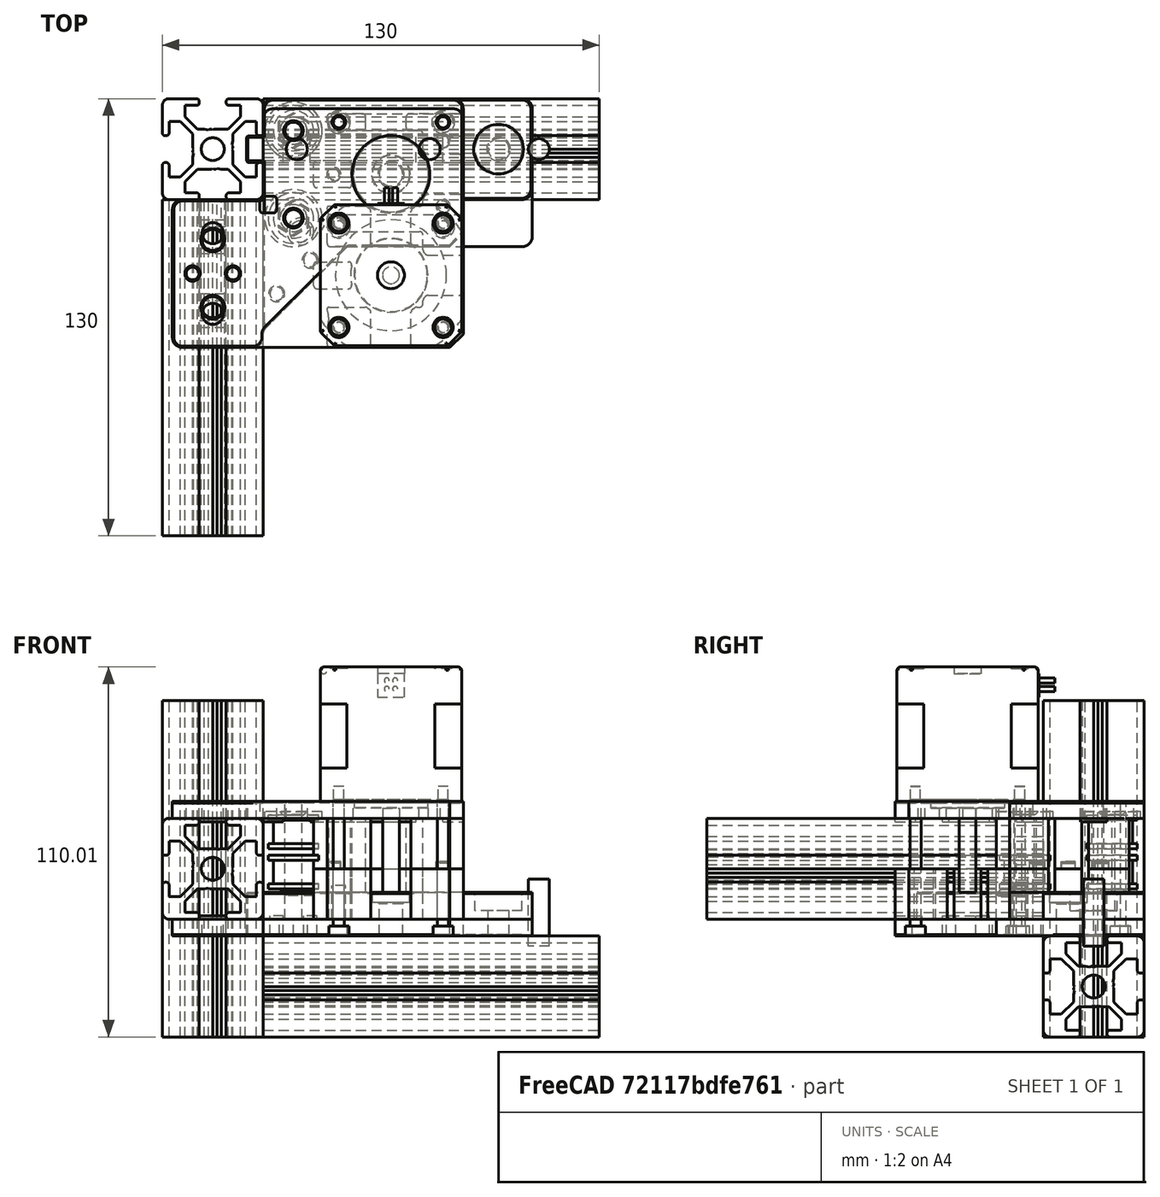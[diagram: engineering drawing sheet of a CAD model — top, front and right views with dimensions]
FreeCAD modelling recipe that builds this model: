
FCSTD DOCUMENT  (FreeCAD 0.19R24366 (Git))
Label: motor-mount-common
License: Other
LicenseURL: GPL3
objects: Part::Cylinder×38, Part::MultiFuse×31, Part::Box×30, Part::Feature×26, Part::Cut×24, Part::Chamfer×18, Part::Fillet×15, App::Part×2, Part::Refine×2, App::DocumentObjectGroup×1
note: 184 computed .brp shape members not serialized (recipe doc carries the construction recipe); baked Part::Feature solids carry a one-line shape summary decoded from their .brp

FEATURE [Part::Feature] Extrude001003002002002002  label="Extrude001003002002004"
  Placement = pos=(-15,-100,15) rot=(-1,0,0;1.5708rad)
  shape: bbox 30 x 100 x 30 mm, 95 faces (baked)
FEATURE [Part::Feature] Extrude001003002002002003  label="Extrude001003002002005"
  Placement = pos=(-2.5e-14,15,-20) rot=(0.57735,-0.57735,0.57735;4.18879rad)
  shape: bbox 100 x 30 x 30 mm, 95 faces (baked)
FEATURE [Part::Feature] Chamfer004  label="btm-support"
  Placement = pos=(11,-9.5,7) rot=(0,0,1;0rad)
  shape: bbox 8 x 8 x 1.85 mm, 4 faces (baked)
FEATURE [Part::Feature] Fusion006002011004053036004001001  label="motor-40mm"
  Placement = pos=(38,-22.5,75) rot=(1,0,0;3.14159rad)
  shape: bbox 42 x 47 x 67 mm, 100 faces (baked)
FEATURE [Part::Cylinder] Cylinder054
  Angle = 360
  AttacherType = Attacher::AttachEngine3D
  Height = 10
  Placement = pos=(22.5,-7,0) rot=(0,0,1;0rad)
  Radius = 2
FEATURE [Part::Box] Box  label="Cube"
  AttacherType = Attacher::AttachEngine3D
  Height = 5
  Length = 86.5
  Placement = pos=(-27,-44,30) rot=(0,0,1;0rad)
  Width = 44
FEATURE [Part::Feature] Cut001  label="smooth-idler-6mm"
  Placement = pos=(9,20.5,21) rot=(0,0,-1;1.5708rad)
  shape: bbox 15 x 15 x 10 mm, 8 faces (baked)
FEATURE [Part::Feature] Cut002005  label="smooth-idler-6mm004"
  Placement = pos=(9,20.5,9) rot=(0,0,-1;1.5708rad)
  shape: bbox 15 x 15 x 10 mm, 8 faces (baked)
FEATURE [Part::Feature] Cut002007  label="smooth-idler-6mm006"
  Placement = pos=(9,-5.5,9) rot=(0,0,-1;1.5708rad)
  shape: bbox 15 x 15 x 10 mm, 8 faces (baked)
FEATURE [App::Part] Part001  label="pref"
  Group = -> [Fusion006002011004053036004001001,Cut001,Cut002005,Cut002007]
  Origin = -> Origin001
FEATURE [Part::Box] Box001  label="Cube001"
  AttacherType = Attacher::AttachEngine3D
  Height = 5
  Length = 59.5
  Placement = pos=(0,0,30) rot=(0,0,1;0rad)
  Width = 27
FEATURE [Part::Box] Box002  label="Cube002"
  AttacherType = Attacher::AttachEngine3D
  Height = 5
  Length = 5
  Placement = pos=(-1,-4,30) rot=(0,0,1;0rad)
  Width = 5
FEATURE [Part::MultiFuse] Fusion
  Shapes = -> [Box,Box001]
FEATURE [Part::Cut] Cut
  Base = -> Fusion
  Tool = -> Box002
FEATURE [Part::Chamfer] Chamfer
  Base = -> Cut
  Edges = 1 edges r=4: [Edge6]
FEATURE [Part::Fillet] Fillet
  Base = -> Chamfer
  Edges = 4 edges r=3: [Edge3,Edge16,Edge38,Edge39]
FEATURE [Part::Fillet] Fillet001  label="base-plate-nh"
  Base = -> Fillet
  Edges = 5 edges r=1: [Edge37,Edge38,Edge40,Edge41,Edge50]
FEATURE [Part::Cylinder] Cylinder
  Angle = 360
  AttacherType = Attacher::AttachEngine3D
  Height = 10
  Placement = pos=(-15,-10,26.5) rot=(0,0,1;0rad)
  Radius = 3.15
FEATURE [Part::Cylinder] Cylinder055
  Angle = 360
  AttacherType = Attacher::AttachEngine3D
  Height = 10
  Placement = pos=(10,15,26.5) rot=(0,0,1;0rad)
  Radius = 3.15
FEATURE [Part::Cylinder] Cylinder056
  Angle = 360
  AttacherType = Attacher::AttachEngine3D
  Height = 10
  Placement = pos=(-15,-34,26.5) rot=(0,0,1;0rad)
  Radius = 3.15
FEATURE [Part::Cylinder] Cylinder057
  Angle = 360
  AttacherType = Attacher::AttachEngine3D
  Height = 10
  Placement = pos=(49.5,15,26.5) rot=(0,0,1;0rad)
  Radius = 3.15
FEATURE [Part::MultiFuse] Fusion006002011004053036004001002
  Shapes = -> [Cylinder057,Cylinder056,Cylinder055,Cylinder]
FEATURE [Part::Box] Box003  label="Cube003"
  AttacherType = Attacher::AttachEngine3D
  Height = 1
  Length = 6
  Placement = pos=(0,11.1,29) rot=(0,0,1;0rad)
  Width = 7.8
FEATURE [Part::Box] Box004  label="Cube004"
  AttacherType = Attacher::AttachEngine3D
  Height = 1
  Length = 6
  Placement = pos=(53.5,11.1,29) rot=(0,0,1;0rad)
  Width = 7.8
FEATURE [Part::Box] Box005  label="Cube005"
  AttacherType = Attacher::AttachEngine3D
  Height = 1
  Length = 31.5
  Placement = pos=(14,11.1,29) rot=(0,0,1;0rad)
  Width = 7.8
FEATURE [Part::Box] Box006  label="Cube006"
  AttacherType = Attacher::AttachEngine3D
  Height = 1
  Length = 7.8
  Placement = pos=(-18.9,-6,29) rot=(0,0,1;0rad)
  Width = 6
FEATURE [Part::Box] Box007  label="Cube007"
  AttacherType = Attacher::AttachEngine3D
  Height = 1
  Length = 7.8
  Placement = pos=(-18.9,-44,29) rot=(0,0,1;0rad)
  Width = 6
FEATURE [Part::Box] Box008  label="Cube008"
  AttacherType = Attacher::AttachEngine3D
  Height = 1
  Length = 7.8
  Placement = pos=(-18.9,-30,29) rot=(0,0,1;0rad)
  Width = 15.5
FEATURE [Part::MultiFuse] Fusion006002011004053036004001003  label="mounting-tab"
  Shapes = -> [Box008,Box007,Box006,Box005,Box004,Box003]
FEATURE [Part::Cut] Cut002008  label="base-plate"
  Base = -> Fillet001
  Tool = -> Fusion006002011004053036004001002
FEATURE [Part::Box] Box009  label="Cube009"
  AttacherType = Attacher::AttachEngine3D
  Height = 8
  Length = 80
  Placement = pos=(0,-14,0) rot=(0,0,1;0rad)
  Width = 44
FEATURE [Part::Feature] Chamfer009  label="btm-support001"
  Placement = pos=(9,20.5,7) rot=(0,0,1;0rad)
  shape: bbox 8 x 8 x 1.85 mm, 4 faces (baked)
FEATURE [Part::Feature] Chamfer010  label="top-support001"
  Placement = pos=(9,20.5,33) rot=(0,0,1;0rad)
  shape: bbox 8 x 8 x 1.85 mm, 4 faces (baked)
FEATURE [Part::Cylinder] Cylinder058
  Angle = 360
  AttacherType = Attacher::AttachEngine3D
  Height = 3
  Placement = pos=(9,20.5,29) rot=(0,0,1;0rad)
  Radius = 8.5
FEATURE [Part::Cylinder] Cylinder059
  Angle = 360
  AttacherType = Attacher::AttachEngine3D
  Height = 4
  Placement = pos=(38,7.5,5) rot=(0,0,1;0rad)
  Radius = 5.55
FEATURE [Part::Cylinder] Cylinder060
  Angle = 360
  AttacherType = Attacher::AttachEngine3D
  Height = 9
  Placement = pos=(38,7.5,28.5) rot=(0,0,1;0rad)
  Radius = 11.15
FEATURE [Part::Cylinder] Cylinder061
  Angle = 360
  AttacherType = Attacher::AttachEngine3D
  Height = 40
  Placement = pos=(22.5,-7,-5) rot=(0,0,1;0rad)
  Radius = 1.65
FEATURE [Part::Cylinder] Cylinder062
  Angle = 360
  AttacherType = Attacher::AttachEngine3D
  Height = 40
  Placement = pos=(53.5,-7,-5) rot=(0,0,1;0rad)
  Radius = 1.65
FEATURE [Part::Cylinder] Cylinder063
  Angle = 360
  AttacherType = Attacher::AttachEngine3D
  Height = 40
  Placement = pos=(22.5,-38,-5) rot=(0,0,1;0rad)
  Radius = 1.65
FEATURE [Part::Cylinder] Cylinder064
  Angle = 360
  AttacherType = Attacher::AttachEngine3D
  Height = 40
  Placement = pos=(53.5,-38,-5) rot=(0,0,1;0rad)
  Radius = 1.65
FEATURE [Part::Cylinder] Cylinder065
  Angle = 360
  AttacherType = Attacher::AttachEngine3D
  Height = 3
  Placement = pos=(22.5,-7,-5) rot=(0,0,1;0rad)
  Radius = 3
FEATURE [Part::Cylinder] Cylinder066
  Angle = 360
  AttacherType = Attacher::AttachEngine3D
  Height = 3
  Placement = pos=(53.5,-7,-5) rot=(0,0,1;0rad)
  Radius = 3
FEATURE [Part::Cylinder] Cylinder067
  Angle = 360
  AttacherType = Attacher::AttachEngine3D
  Height = 3
  Placement = pos=(22.5,-38,-5) rot=(0,0,1;0rad)
  Radius = 3
FEATURE [Part::Cylinder] Cylinder068
  Angle = 360
  AttacherType = Attacher::AttachEngine3D
  Height = 3
  Placement = pos=(53.5,-38,-5) rot=(0,0,1;0rad)
  Radius = 3
FEATURE [Part::MultiFuse] Fusion006002011004053036004001003009  label="motor-bolt"
  Shapes = -> [Cylinder068,Cylinder067,Cylinder066,Cylinder065,Cylinder061,Cylinder062,Cylinder063,Cylinder064]
FEATURE [Part::Box] Box011  label="Cube011"
  AttacherType = Attacher::AttachEngine3D
  Height = 15
  Length = 13
  Placement = pos=(19,-44,0) rot=(0,0,1;0rad)
  Width = 12
FEATURE [Part::Box] Box012  label="Cube012"
  AttacherType = Attacher::AttachEngine3D
  Height = 15
  Length = 15.5
  Placement = pos=(44,-44,0) rot=(0,0,1;0rad)
  Width = 12
FEATURE [Part::Box] Box013  label="Cube013"
  AttacherType = Attacher::AttachEngine3D
  Height = 15
  Length = 40.5
  Placement = pos=(19,-9.5,0) rot=(0,0,1;0rad)
  Width = 5
FEATURE [Part::Box] Box014  label="Cube014"
  AttacherType = Attacher::AttachEngine3D
  Height = 15
  Length = 12
  Placement = pos=(47.5,-32,0) rot=(0,0,1;0rad)
  Width = 3.5
FEATURE [Part::Chamfer] Chamfer012
  Base = -> Box012
  Edges = 1 edges r=4: [Edge5]
FEATURE [Part::Box] Box015  label="Cube015"
  AttacherType = Attacher::AttachEngine3D
  Height = 15
  Length = 12
  Placement = pos=(47.5,-16.5,0) rot=(0,0,1;0rad)
  Width = 7
FEATURE [Part::Cylinder] Cylinder069
  Angle = 360
  AttacherType = Attacher::AttachEngine3D
  Height = 15
  Placement = pos=(11,-35.5,0) rot=(0,0,1;0rad)
  Radius = 8.5
FEATURE [Part::Cylinder] Cylinder070
  Angle = 360
  AttacherType = Attacher::AttachEngine3D
  Height = 15
  Placement = pos=(38,-22.5,0) rot=(0,0,1;0rad)
  Radius = 12
FEATURE [Part::Cylinder] Cylinder071
  Angle = 360
  AttacherType = Attacher::AttachEngine3D
  Height = 15
  Placement = pos=(11,-9.5,0) rot=(0,0,1;0rad)
  Radius = 8.5
FEATURE [Part::MultiFuse] Fusion006002011004053036004001003011
  Shapes = -> [Cylinder070,Cylinder069,Cylinder071]
FEATURE [Part::Box] Box016  label="Cube016"
  AttacherType = Attacher::AttachEngine3D
  Height = 15
  Length = 14.5
  Placement = pos=(15,-26.5,0) rot=(0,0,1;0rad)
  Width = 8
FEATURE [Part::MultiFuse] Fusion006002011004053036004001003012
  Shapes = -> [Box013,Box015,Box014,Chamfer012,Box011,Box016]
FEATURE [Part::Cut] Cut002008008
  Base = -> Fusion006002011004053036004001003012
  Tool = -> Fusion006002011004053036004001003011
FEATURE [Part::Fillet] Fillet003
  Base = -> Cut002008008
  Edges = 1 edges r=0.5: [Edge83]
FEATURE [Part::Fillet] Fillet004  label="wall"
  Base = -> Fillet003
  Edges = 23 edges r=1: [Edge18,Edge21,Edge24,Edge26,Edge29,Edge31,Edge38,Edge43,Edge49,Edge54,Edge55,Edge56,Edge58,Edge60,Edge65,Edge72,Edge73,Edge85,Edge88,Edge89,Edge91,Edge94,Edge99]
FEATURE [App::DocumentObjectGroup] Group  label="Base"
  Group = -> [Cut002008,Fusion006002011004053036004001003,Fillet004,Fusion006002011004053036004001003009]
FEATURE [Part::Cylinder] Cylinder072
  Angle = 360
  AttacherType = Attacher::AttachEngine3D
  Height = 2.2
  Placement = pos=(21,-22.5,15) rot=(0,0,1;0rad)
  Radius = 2.1
FEATURE [Part::Cylinder] Cylinder073
  Angle = 360
  AttacherType = Attacher::AttachEngine3D
  Height = 2.2
  Placement = pos=(53.5,-32,15) rot=(0,0,1;0rad)
  Radius = 2.1
FEATURE [Part::Cylinder] Cylinder074
  Angle = 360
  AttacherType = Attacher::AttachEngine3D
  Height = 2.2
  Placement = pos=(53.5,-12.5,15) rot=(0,0,1;0rad)
  Radius = 2.1
FEATURE [Part::Cylinder] Cylinder075
  Angle = 360
  AttacherType = Attacher::AttachEngine3D
  Height = 2
  Placement = pos=(53.5,-12.5,15) rot=(0,0,1;0rad)
  Radius = 2
FEATURE [Part::Cylinder] Cylinder076
  Angle = 360
  AttacherType = Attacher::AttachEngine3D
  Height = 2
  Placement = pos=(53.5,-32,15) rot=(0,0,1;0rad)
  Radius = 2
FEATURE [Part::Cylinder] Cylinder077
  Angle = 360
  AttacherType = Attacher::AttachEngine3D
  Height = 2
  Placement = pos=(21,-22.5,15) rot=(0,0,1;0rad)
  Radius = 2
FEATURE [Part::MultiFuse] Fusion006002011004053036004001003013
  Shapes = -> [Cylinder077,Cylinder076,Cylinder075]
FEATURE [Part::Chamfer] Chamfer013
  Base = -> Fusion006002011004053036004001003013
  Edges = 3 edges r=0.4: [Edge1,Edge4,Edge7]
FEATURE [Part::MultiFuse] Fusion006002011004053036004001003014
  Shapes = -> [Cylinder074,Cylinder072,Cylinder073]
FEATURE [Part::Feature] Fillet004001  label="wall001"
  shape: bbox 44.5 x 39.5 x 15 mm, 60 faces, 4 solids (baked)
FEATURE [Part::Feature] Fillet004002  label="wall002"
  Placement = pos=(0,0,15) rot=(0,0,1;0rad)
  shape: bbox 44.5 x 39.5 x 15 mm, 60 faces, 4 solids (baked)
FEATURE [Part::Cut] Cut002008009  label="upper-wall"
  Base = -> Fillet004002
  Placement = pos=(0,30,0) rot=(0,0,1;0rad)
  Tool = -> Fusion006002011004053036004001003014
FEATURE [Part::Feature] Fusion006002011004053036004001003009001  label="motor-bolt001"
  Placement = pos=(0,30,0) rot=(0,0,1;0rad)
  shape: bbox 37 x 37 x 40 mm, 20 faces, 4 solids (baked)
FEATURE [Part::Feature] Fusion006002011004053036004001003009002  label="motor-bolt002"
  Placement = pos=(0,30,0) rot=(0,0,1;0rad)
  shape: bbox 37 x 37 x 40 mm, 20 faces, 4 solids (baked)
FEATURE [Part::Feature] Chamfer015  label="btm-support002"
  Placement = pos=(9,-5.5,7) rot=(0,0,1;0rad)
  shape: bbox 8 x 8 x 1.85 mm, 4 faces (baked)
FEATURE [Part::Cylinder] Cylinder078
  Angle = 360
  AttacherType = Attacher::AttachEngine3D
  Height = 10
  Placement = pos=(9,-5.5,22) rot=(0,0,1;0rad)
  Radius = 8.5
FEATURE [Part::Feature] Chamfer014  label="top-support002"
  Placement = pos=(9,-5.5,33) rot=(0,0,1;0rad)
  shape: bbox 8 x 8 x 1.85 mm, 4 faces (baked)
FEATURE [Part::Cylinder] Cylinder079
  Angle = 360
  AttacherType = Attacher::AttachEngine3D
  Height = 44
  Placement = pos=(9,20.5,-10) rot=(0,0,1;0rad)
  Radius = 2.525
FEATURE [Part::Cylinder] Cylinder080
  Angle = 360
  AttacherType = Attacher::AttachEngine3D
  Height = 44
  Placement = pos=(9,-5.5,-10) rot=(0,0,1;0rad)
  Radius = 2.525
FEATURE [Part::Feature] Fusion006002011004053036004001003009006001  label="Fusion006002011004053036004001003009007"
  Placement = pos=(-2,30,-7) rot=(0,0,1;0rad)
  shape: bbox 5.05 x 31.05 x 44 mm, 6 faces, 2 solids (baked)
FEATURE [Part::Feature] Body001  label="m5-nut-slot"
  Placement = pos=(9,20.5,-5) rot=(0,0,1;0rad)
  shape: bbox 8.4 x 9.7 x 4 mm, 8 faces (baked)
FEATURE [Part::Feature] Body002  label="m5-nut-slot001"
  Placement = pos=(9,-5.5,-5) rot=(0,0,1;0rad)
  shape: bbox 8.4 x 9.7 x 4 mm, 8 faces (baked)
FEATURE [Part::Feature] Extrude001003002002002001  label="Extrude001003002002003"
  Placement = pos=(-15,15,-35) rot=(0,0,1;0rad)
  shape: bbox 30 x 30 x 100 mm, 95 faces (baked)
FEATURE [App::Part] Part  label="extrusion"
  Group = -> [Extrude001003002002002001,Extrude001003002002002002,Extrude001003002002002003]
  Origin = -> Origin
FEATURE [Part::Box] Box018  label="Cube018"
  AttacherType = Attacher::AttachEngine3D
  Height = 5
  Length = 27
  Placement = pos=(-27,-44,-5) rot=(0,0,1;0rad)
  Width = 44
FEATURE [Part::Box] Box019  label="Cube019"
  AttacherType = Attacher::AttachEngine3D
  Height = 5
  Length = 80
  Placement = pos=(0,-14,-5) rot=(0,0,1;0rad)
  Width = 44
FEATURE [Part::MultiFuse] Fusion006002011004053036004001003009006003
  Shapes = -> [Box019,Box018]
FEATURE [Part::Chamfer] Chamfer016
  Base = -> Fusion006002011004053036004001003009006003
  Edges = 1 edges r=25: [Edge21]
FEATURE [Part::Fillet] Fillet004003
  Base = -> Chamfer016
  Edges = 6 edges r=3: [Edge10,Edge13,Edge20,Edge25,Edge28,Edge29]
FEATURE [Part::Box] Box020  label="Cube020"
  AttacherType = Attacher::AttachEngine3D
  Height = 8
  Length = 26
  Placement = pos=(-1,-39,0) rot=(0,0,1;0rad)
  Width = 26
FEATURE [Part::Box] Box021  label="Cube021"
  AttacherType = Attacher::AttachEngine3D
  Height = 8
  Length = 26
  Placement = pos=(-26,-39,0) rot=(0,0,1;0rad)
  Width = 26
FEATURE [Part::Chamfer] Chamfer017
  Base = -> Box020
  Edges = 1 edges r=25: [Edge5]
FEATURE [Part::Cut] Cut002008010
  Base = -> Chamfer017
  Tool = -> Box021
FEATURE [Part::Fillet] Fillet004003004
  Base = -> Cut002008010
  Edges = 1 edges r=1: [Edge9]
FEATURE [Part::MultiFuse] Fusion006002011004053036004001003009006004
  Shapes = -> [Fillet004003004,Box009]
FEATURE [Part::Fillet] Fillet004003005
  Base = -> Fusion006002011004053036004001003009006004
  Edges = 1 edges r=1.99: [Edge20]
FEATURE [Part::Box] Box022  label="Cube022"
  AttacherType = Attacher::AttachEngine3D
  Height = 5
  Length = 6
  Placement = pos=(-5,11.1,-5) rot=(0,0,1;0rad)
  Width = 7.8
FEATURE [Part::Box] Box023  label="Cube023"
  AttacherType = Attacher::AttachEngine3D
  Height = 8
  Length = 6
  Placement = pos=(-5,11.1,0) rot=(0,0,1;0rad)
  Width = 7.8
FEATURE [Part::Chamfer] Chamfer018
  Base = -> Box023
  Edges = 2 edges r=0.4: [Edge1,Edge3]
FEATURE [Part::Chamfer] Chamfer019
  Base = -> Box022
  Edges = 2 edges r=0.4: [Edge1,Edge3]
FEATURE [Part::Feature] Fusion006002011004053036004001003009006006001  label="base-plate002"
  Placement = pos=(0,0,35) rot=(0,0,1;0rad)
  shape: bbox 107 x 74 x 5 mm, 30 faces (baked)
FEATURE [Part::Box] Box024  label="Cube024"
  AttacherType = Attacher::AttachEngine3D
  Height = 10
  Length = 27
  Placement = pos=(59.5,-15,26) rot=(0,0,1;0rad)
  Width = 46
FEATURE [Part::Cut] Cut002008011
  Base = -> Fusion006002011004053036004001003009006006001
  Tool = -> Box024
FEATURE [Part::Chamfer] Chamfer021
  Base = -> Cut002008011
  Edges = 1 edges r=4: [Edge44]
FEATURE [Part::Fillet] Fillet004003007
  Base = -> Chamfer021
  Edges = 1 edges r=3: [Edge29]
FEATURE [Part::Box] Box025  label="Cube025"
  AttacherType = Attacher::AttachEngine3D
  Height = 1
  Length = 7.8
  Placement = pos=(-18.9,-44,0) rot=(0,0,1;0rad)
  Width = 8
FEATURE [Part::Cylinder] Cylinder081
  Angle = 360
  AttacherType = Attacher::AttachEngine3D
  Height = 47
  Placement = pos=(-15,-12,0) rot=(0,0,1;0rad)
  Radius = 3.15
FEATURE [Part::Cylinder] Cylinder082
  Angle = 360
  AttacherType = Attacher::AttachEngine3D
  Height = 47
  Placement = pos=(-15,-32,0) rot=(0,0,1;0rad)
  Radius = 3.15
FEATURE [Part::Box] Box026  label="Cube026"
  AttacherType = Attacher::AttachEngine3D
  Height = 1
  Length = 7.8
  Placement = pos=(-18.9,-28,0) rot=(0,0,1;0rad)
  Width = 12
FEATURE [Part::Box] Box027  label="Cube027"
  AttacherType = Attacher::AttachEngine3D
  Height = 1
  Length = 7.8
  Placement = pos=(-18.9,-8,0) rot=(0,0,1;0rad)
  Width = 8
FEATURE [Part::MultiFuse] Fusion006002011004053036004001003009006006002  label="mounting-tab001"
  Shapes = -> [Box027,Box026,Box025]
FEATURE [Part::MultiFuse] Fusion006002011004053036004001003009006006003
  Placement = pos=(0,0,-15) rot=(0,0,1;0rad)
  Shapes = -> [Cylinder081,Cylinder082]
FEATURE [Part::Feature] Fusion006002011004053036004001003009006006003001  label="Fusion006002011004053036004001003009006006004"
  shape: bbox 6.3 x 26.3 x 47 mm, 6 faces, 2 solids (baked)
FEATURE [Part::Feature] Fusion006002011004053036004001003009006006002001  label="mounting-tab002"
  Placement = pos=(0,0,29) rot=(0,0,1;0rad)
  shape: bbox 7.8 x 44 x 1 mm, 18 faces, 3 solids (baked)
FEATURE [Part::MultiFuse] Fusion006002011004053036004001003009006006003003
  Shapes = -> [Fusion006002011004053036004001003009006006002001,Fillet004003007]
FEATURE [Part::Cut] Cut002008013
  Base = -> Fusion006002011004053036004001003009006006003003
  Tool = -> Fusion006002011004053036004001003009006006003001
FEATURE [Part::Cylinder] Cylinder083
  Angle = 360
  AttacherType = Attacher::AttachEngine3D
  Height = 19
  Placement = pos=(70,15,-8.5) rot=(0,0,1;0rad)
  Radius = 3.1
FEATURE [Part::Box] Box028  label="Cube028"
  AttacherType = Attacher::AttachEngine3D
  Height = 22
  Length = 27
  Placement = pos=(59.5,-14,-7.5) rot=(0,0,1;0rad)
  Width = 14
FEATURE [Part::Box] Box029  label="Cube029"
  AttacherType = Attacher::AttachEngine3D
  Height = 22
  Length = 27
  Placement = pos=(59.5,-14,-7.5) rot=(0,0,1;0rad)
  Width = 14
FEATURE [Part::Cylinder] Cylinder084
  Angle = 360
  AttacherType = Attacher::AttachEngine3D
  Height = 20
  Placement = pos=(82,15,-8) rot=(0,0,1;0rad)
  Radius = 3.1
FEATURE [Part::MultiFuse] Fusion006002011004053036004001003015  label="lower-wall"
  Placement = pos=(0,30,0) rot=(0,0,1;0rad)
  Shapes = -> [Fillet004001,Chamfer013]
FEATURE [Part::Feature] Fillet004003001  label="Fillet004004"
  shape: bbox 107 x 74 x 5 mm, 17 faces (baked)
FEATURE [Part::Fillet] Fillet004003002
  Base = -> Fillet004003001
  Edges = 2 edges r=1.99: [Edge3,Edge9]
FEATURE [Part::Fillet] Fillet004003003
  Base = -> Fillet004003002
  Edges = 1 edges r=1: [Edge48]
FEATURE [Part::MultiFuse] Fusion006002011004053036004001003009006006  label="base-plate001"
  Shapes = -> [Fillet004003003,Chamfer019]
FEATURE [Part::MultiFuse] Fusion006002011004053036004001003009006006003002
  Shapes = -> [Fusion006002011004053036004001003009006006002,Fusion006002011004053036004001003009006006]
FEATURE [Part::Cut] Cut002008014
  Base = -> Fusion006002011004053036004001003009006006003002
  Tool = -> Fusion006002011004053036004001003009006006003
FEATURE [Part::Fillet] Fillet004003006
  Base = -> Fillet004003005
  Edges = 3 edges r=3: [Edge26,Edge27,Edge30]
FEATURE [Part::Cut] Cut002008023012003
  Base = -> Fillet004003006
  Tool = -> Box028
FEATURE [Part::Cut] Cut002008023012004
  Base = -> Cut002008014
  Tool = -> Box029
FEATURE [Part::Chamfer] Chamfer033
  Base = -> Cut002008023012003
  Edges = 1 edges r=4: [Edge34]
FEATURE [Part::Chamfer] Chamfer034
  Base = -> Cut002008023012004
  Edges = 1 edges r=4: [Edge53]
FEATURE [Part::Fillet] Fillet004003008
  Base = -> Chamfer033
  Edges = 1 edges r=3: [Edge20]
FEATURE [Part::Fillet] Fillet004003009
  Base = -> Chamfer034
  Edges = 1 edges r=3: [Edge38]
FEATURE [Part::Feature] Fillet004003008001  label="Fillet004003010"
  shape: bbox 80 x 67.59 x 8 mm, 15 faces (baked)
FEATURE [Part::Chamfer] Chamfer035
  Base = -> Fillet004003008001
  Edges = 13 edges r=0.4: [Edge4,Edge7,Edge8,Edge11,Edge16,Edge19,Edge22,Edge25,Edge28,Edge31,Edge34,Edge37,Edge38]
FEATURE [Part::Cylinder] Cylinder085
  Angle = 360
  AttacherType = Attacher::AttachEngine3D
  Height = 19
  Placement = pos=(70,15,2.5) rot=(0,0,1;0rad)
  Radius = 7
FEATURE [Part::MultiFuse] Fusion006002011004053036004001003009006006003012
  Shapes = -> [Cylinder085,Cylinder083]
FEATURE [Part::Chamfer] Chamfer038
  Base = -> Chamfer018
  Edges = 5 edges r=0.4: [Edge1,Edge5,Edge6,Edge7,Edge8]
FEATURE [Part::MultiFuse] Fusion006002011004053036004001003009006006003013
  Shapes = -> [Chamfer035,Chamfer038]
FEATURE [Part::MultiFuse] Fusion006002011004053036004001003009006006003014
  Shapes = -> [Fillet004003009,Fusion006002011004053036004001003009006006003013]
FEATURE [Part::MultiFuse] Fusion006002011004053036004001003009006006003015
  Shapes = -> [Fusion006002011004053036004001003009006006003014,Fusion006002011004053036004001003015]
FEATURE [Part::MultiFuse] Fusion006002011004053036004001003009006006003016
  Shapes = -> [Chamfer015,Chamfer009]
FEATURE [Part::MultiFuse] Fusion006002011004053036004001003009006006003017
  Shapes = -> [Fusion006002011004053036004001003009006006003015,Fusion006002011004053036004001003009006006003016]
FEATURE [Part::Cut] Cut002008023012005
  Base = -> Fusion006002011004053036004001003009006006003017
  Tool = -> Cylinder059
FEATURE [Part::MultiFuse] Fusion006002011004053036004001003009006006003018
  Shapes = -> [Body001,Body002]
FEATURE [Part::MultiFuse] Fusion006002011004053036004001003009006006003019
  Shapes = -> [Cylinder080,Cylinder079]
FEATURE [Part::Cut] Cut002008023012006
  Base = -> Cut002008023012005
  Tool = -> Fusion006002011004053036004001003009006006003019
FEATURE [Part::Cut] Cut002008023012007
  Base = -> Cut002008023012006
  Tool = -> Fusion006002011004053036004001003009001
FEATURE [Part::Cut] Cut002008023012008
  Base = -> Cut002008023012007
  Tool = -> Fusion006002011004053036004001003009006006003012
FEATURE [Part::Chamfer] Chamfer039
  Base = -> Cut002008023012008
  Edges = 1 edges r=0.2: [Edge280]
FEATURE [Part::Chamfer] Chamfer040
  Base = -> Chamfer039
  Edges = 1 edges r=0.4: [Edge67]
FEATURE [Part::MultiFuse] Fusion006002011004053036004001003009006006003020
  Shapes = -> [Cylinder078,Cylinder058]
FEATURE [Part::Cut] Cut002008023012009002
  Base = -> Cut002008013
  Tool = -> Fusion006002011004053036004001003009006006003020
FEATURE [Part::MultiFuse] Fusion006002011004053036004001003009006006003021
  Shapes = -> [Chamfer014,Chamfer010]
FEATURE [Part::MultiFuse] Fusion006002011004053036004001003009006006003022
  Shapes = -> [Cut002008023012009002,Fusion006002011004053036004001003009006006003021]
FEATURE [Part::Cut] Cut002008023012009003
  Base = -> Fusion006002011004053036004001003009006006003022
  Tool = -> Fusion006002011004053036004001003009006001
FEATURE [Part::Cut] Cut002008023012009005
  Base = -> Cut002008023012009003
  Tool = -> Cylinder060
FEATURE [Part::MultiFuse] Fusion006002011004053036004001003009006006003023
  Shapes = -> [Cut002008009,Cut002008023012009005]
FEATURE [Part::Cylinder] Cylinder086
  Angle = 360
  AttacherType = Attacher::AttachEngine3D
  Height = 6
  Placement = pos=(13,-19,-5) rot=(0,0,1;0rad)
  Radius = 2
FEATURE [Part::Cylinder] Cylinder087
  Angle = 360
  AttacherType = Attacher::AttachEngine3D
  Height = 6
  Placement = pos=(3,-29,-5) rot=(0,0,1;0rad)
  Radius = 2
FEATURE [Part::MultiFuse] Fusion006002011004053036004001003009006006003024
  Placement = pos=(1,1,0) rot=(0,0,1;0rad)
  Shapes = -> [Cylinder087,Cylinder086]
FEATURE [Part::Cylinder] Cylinder090
  Angle = 360
  AttacherType = Attacher::AttachEngine3D
  Height = 10
  Placement = pos=(-21,-22,35) rot=(0,0,1;0rad)
  Radius = 1.9
FEATURE [Part::Cylinder] Cylinder091
  Angle = 360
  AttacherType = Attacher::AttachEngine3D
  Height = 10
  Placement = pos=(-9,-22,35) rot=(0,0,1;0rad)
  Radius = 1.9
FEATURE [Part::MultiFuse] Fusion006002011004053036004001003009006006003025
  Placement = pos=(0,0,-5) rot=(0,0,1;0rad)
  Shapes = -> [Cylinder091,Cylinder090]
FEATURE [Part::Feature] Cut002008023012009006003002001  label="Cut002008023012009006003003"
  shape: bbox 86.5 x 74 x 20 mm, 140 faces (baked)
FEATURE [Part::Box] Box030  label="Cube030"
  AttacherType = Attacher::AttachEngine3D
  Height = 22
  Length = 12
  Placement = pos=(30.5,20.5,8) rot=(0,0,1;0rad)
  Width = 5
FEATURE [Part::Box] Box031  label="Cube031"
  AttacherType = Attacher::AttachEngine3D
  Height = 22
  Length = 12
  Placement = pos=(30.5,20.5,8) rot=(0,0,1;0rad)
  Width = 5
FEATURE [Part::Feature] Fusion006002011004053036004001003009006006003018001
  Placement = pos=(0,0,1) rot=(0,0,1;0rad)
  shape: bbox 8.4 x 35.7 x 4 mm, 16 faces, 2 solids (baked)
FEATURE [Part::MultiFuse] Fusion006002011004053036004001003009006006003018002
  Shapes = -> [Fusion006002011004053036004001003009006006003018001,Fusion006002011004053036004001003009006006003018]
FEATURE [Part::Cut] Cut002008023012009006003002003
  Base = -> Chamfer040
  Tool = -> Fusion006002011004053036004001003009006006003018002
FEATURE [Part::Cut] Cut002008023012009006003002004
  Base = -> Cut002008023012009006003002003
  Tool = -> Fusion006002011004053036004001003009006006003024
FEATURE [Part::Cut] Cut002008023012009006003002005
  Base = -> Cut002008023012009006003002004
  Tool = -> Box031
FEATURE [Part::Fillet] Fillet004003008003  label="btm-basic"
  Base = -> Cut002008023012009006003002005
  Edges = 4 edges r=1: [Edge191,Edge194,Edge198,Edge199]
FEATURE [Part::Cut] Cut002008023012009006003002006
  Base = -> Fusion006002011004053036004001003009006006003023
  Tool = -> Fusion006002011004053036004001003009002
FEATURE [Part::Cut] Cut002008023012009006003002007
  Base = -> Cut002008023012009006003002006
  Tool = -> Fusion006002011004053036004001003009006006003025
FEATURE [Part::Cut] Cut002008023012009006003002008
  Base = -> Cut002008023012009006003002007
  Tool = -> Box030
FEATURE [Part::Fillet] Fillet004003008004  label="top-basic"
  Base = -> Cut002008023012009006003002008
  Edges = 4 edges r=1: [Edge140,Edge145,Edge163,Edge166]
FEATURE [Part::Refine] Fillet004003008004001  label="top-basic001"
  Source = -> Fillet004003008004
FEATURE [Part::Refine] Fillet004003008003001  label="btm-basic001"
  Source = -> Fillet004003008003
FEATURE [Part::Chamfer] Chamfer041
  Base = -> Fillet004003008004001
  Edges = 25 edges r=0.4: [Edge202,Edge204,Edge206,Edge209,Edge210,Edge221,Edge223,Edge225,Edge235,Edge239,Edge241,Edge242,Edge244,Edge247,Edge248,Edge250,Edge252,Edge256,Edge257,Edge258,Edge334,Edge336,Edge337,Edge339,Edge340]
FEATURE [Part::Chamfer] Chamfer042
  Base = -> Fillet004003008003001
  Edges = 39 edges r=0.4: [Edge216,Edge220,Edge221,Edge230,Edge233,Edge235,Edge244,Edge381,Edge384,Edge386,Edge387,Edge389,Edge391,Edge393,Edge395,Edge398,Edge401,Edge404,Edge405,Edge407,Edge408,Edge409,Edge410,Edge411,Edge412,Edge413,Edge414,Edge415,Edge416,Edge417,Edge418,Edge419,Edge420,Edge421,Edge422,Edge423,Edge424,+2 more]
FEATURE [Part::Cylinder] Cylinder092
  Angle = 360
  AttacherType = Attacher::AttachEngine3D
  Height = 13
  Placement = pos=(38,7.5,-6.5) rot=(0,0,1;0rad)
  Radius = 3.5
FEATURE [Part::Cut] Cut002008023012009006003002009
  Base = -> Chamfer042
  Tool = -> Cylinder092
FEATURE [Part::Chamfer] Chamfer043
  Base = -> Cut002008023012009006003002009
  Edges = 11 edges r=0.4: [Edge85,Edge87,Edge120,Edge121,Edge122,Edge123,Edge130,Edge131,Edge132,Edge133,Edge288]
FEATURE [Part::Chamfer] Chamfer044
  Base = -> Chamfer041
  Edges = 10 edges r=0.4: [Edge148,Edge149,Edge150,Edge151,Edge152,Edge153,Edge154,Edge155,Edge156,Edge157]
